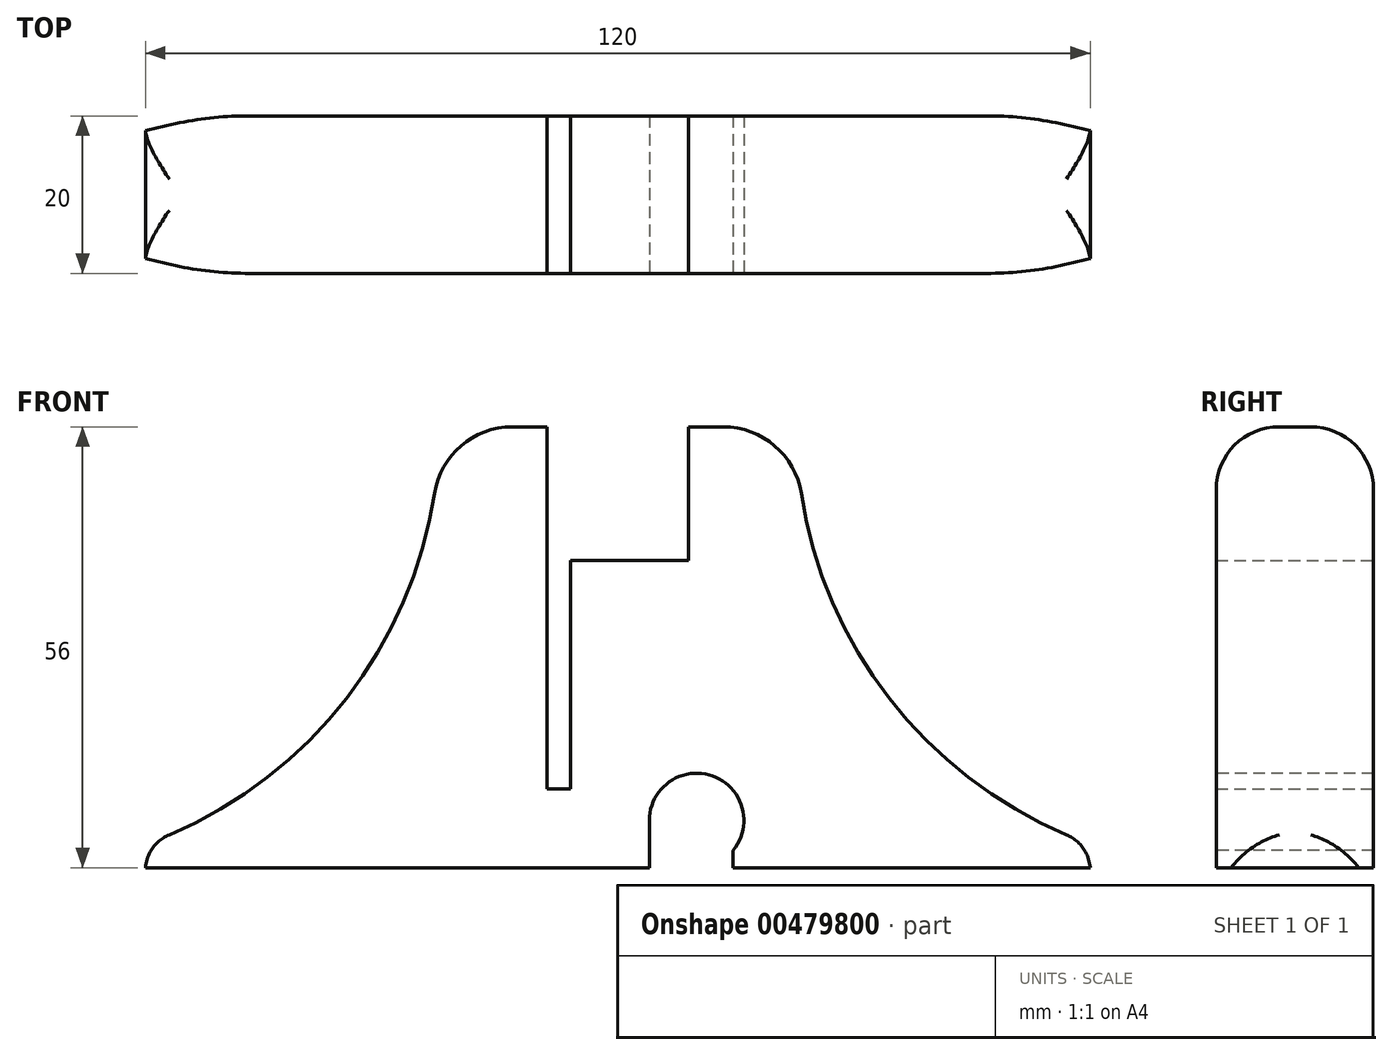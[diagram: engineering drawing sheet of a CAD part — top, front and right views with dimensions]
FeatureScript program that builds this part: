
annotation { "Feature Type Name" : "Feature", "Feature Type Description" : "" }
export const myFeature = defineFeature(function(context is Context, id is Id, definition is map)
    precondition{}
    {
        {
            var Q0;
            Q0=qCreatedBy(makeId("Front.planeOp"),FACE);
            var sketch = newSketch(context, id + "F0", { "sketchPlane" : qUnion([Q0])});
            skLineSegment(sketch, "E0", {"start": v(-9, 56) * mm, "end": v(-9, 10) * mm});
            skLineSegment(sketch, "E1", {"start": v(-9, 10) * mm, "end": v(-6, 10) * mm});
            skLineSegment(sketch, "E2", {"start": v(-6, 10) * mm, "end": v(-6, 39) * mm});
            skLineSegment(sketch, "E3", {"start": v(-6, 39) * mm, "end": v(9, 39) * mm});
            skLineSegment(sketch, "E4", {"start": v(9, 39) * mm, "end": v(9, 56) * mm});
            skLineSegment(sketch, "E5", {"start": v(9, 56) * mm, "end": v(22.65, 56) * mm});
            skLineSegment(sketch, "E6", {"start": v(-9, 56) * mm, "end": v(-22.65, 56) * mm});
            skLineSegment(sketch, "E7", {"start": v(-60, 3) * mm, "end": v(-60, 0) * mm});
            skLineSegment(sketch, "E8", {"start": v(-60, 0) * mm, "end": v(60, 0) * mm});
            skLineSegment(sketch, "E9", {"start": v(60, 0) * mm, "end": v(60, 3) * mm});
            skArc(sketch, "E10", {"start": v(-60, 3) * mm, "mid": v(-32.92, 23.58) * mm, "end": v(-22.65, 56) * mm});
            skArc(sketch, "E11.MirrorC", {"start": v(60, 3) * mm, "mid": v(32.92, 23.58) * mm, "end": v(22.65, 56) * mm});
            skSolve(sketch);
        }
        {
            var Q0;
            Q0 = qSketchRegion(id + "F0", true);
            extrude(context, id + "F1", {"entities" : qUnion([Q0]), "depth" : 20 * mm});
        }
        {
            var Q0;
            Q0=makeQuery(id+"F1.opExtrude","SWEPT_EDGE",EDGE,{"disambiguationData":[OSD([sQuery(id+"F0.wireOp",EDGE,"E6"),sQuery(id+"F0.wireOp",EDGE,"E10")])]});
            var Q1;
            Q1=makeQuery(id+"F1.opExtrude","SWEPT_EDGE",EDGE,{"disambiguationData":[OSD([sQuery(id+"F0.wireOp",EDGE,"E5"),sQuery(id+"F0.wireOp",EDGE,"E11.MirrorC")])]});
            fillet(context, id + "F2", {"entities" : qUnion([Q0, Q1]), "radius" : 10 * mm, "tangentPropagation" : true, "allowEdgeOverflow" : false});
        }
        {
            var Q0;
            Q0=makeQuery(id+"F1.opExtrude","SWEPT_EDGE",EDGE,{"disambiguationData":[OSD([sQuery(id+"F0.wireOp",EDGE,"E7"),sQuery(id+"F0.wireOp",EDGE,"E10")])]});
            var Q1;
            Q1=makeQuery(id+"F1.opExtrude","SWEPT_EDGE",EDGE,{"disambiguationData":[OSD([sQuery(id+"F0.wireOp",EDGE,"E9"),sQuery(id+"F0.wireOp",EDGE,"E11.MirrorC")])]});
            fillet(context, id + "F3", {"entities" : qUnion([Q0, Q1]), "radius" : 5 * mm, "tangentPropagation" : true, "allowEdgeOverflow" : false});
        }
        {
            var Q0;
            {var subQ0=sQuery(id+"F0.wireOp",EDGE,"E10");var subQ1=sQuery(id+"F0.wireOp",EDGE,"E7");Q0=makeQuery(id+"F3.opFillet","BLEND_EDGE",EDGE,{"blendedFrom":[makeQuery(id+"F1.opExtrude","SWEPT_EDGE",EDGE,{"disambiguationData":[OSD([subQ1,subQ0])]}),makeQuery(id+"F1.opExtrude","CAP_FACE",FACE,{"disambiguationData":[OSD([sQuery(id+"F0.wireOp",EDGE,"E0"),sQuery(id+"F0.wireOp",EDGE,"E1"),sQuery(id+"F0.wireOp",EDGE,"E2"),sQuery(id+"F0.wireOp",EDGE,"E3"),sQuery(id+"F0.wireOp",EDGE,"E4"),sQuery(id+"F0.wireOp",EDGE,"E5"),sQuery(id+"F0.wireOp",EDGE,"E6"),subQ1,sQuery(id+"F0.wireOp",EDGE,"E8"),sQuery(id+"F0.wireOp",EDGE,"E9"),subQ0,sQuery(id+"F0.wireOp",EDGE,"E11.MirrorC")])],"isStart":false})],"blendedInto":[makeQuery(id+"F1.opExtrude","CAP_FACE",FACE,{"disambiguationData":[OSD([sQuery(id+"F0.wireOp",EDGE,"E0"),sQuery(id+"F0.wireOp",EDGE,"E1"),sQuery(id+"F0.wireOp",EDGE,"E2"),sQuery(id+"F0.wireOp",EDGE,"E3"),sQuery(id+"F0.wireOp",EDGE,"E4"),sQuery(id+"F0.wireOp",EDGE,"E5"),sQuery(id+"F0.wireOp",EDGE,"E6"),subQ1,sQuery(id+"F0.wireOp",EDGE,"E8"),sQuery(id+"F0.wireOp",EDGE,"E9"),subQ0,sQuery(id+"F0.wireOp",EDGE,"E11.MirrorC")])],"isStart":false})]});}
            var Q1;
            Q1=makeQuery(id+"F1.opExtrude","CAP_EDGE",EDGE,{"disambiguationData":[OSD([sQuery(id+"F0.wireOp",EDGE,"E10")])],"isStart":false});
            var Q2;
            {var subQ0=sQuery(id+"F0.wireOp",EDGE,"E10");var subQ1=sQuery(id+"F0.wireOp",EDGE,"E6");Q2=makeQuery(id+"F2.opFillet","BLEND_EDGE",EDGE,{"blendedFrom":[makeQuery(id+"F1.opExtrude","SWEPT_EDGE",EDGE,{"disambiguationData":[OSD([subQ1,subQ0])]}),makeQuery(id+"F1.opExtrude","CAP_FACE",FACE,{"disambiguationData":[OSD([sQuery(id+"F0.wireOp",EDGE,"E0"),sQuery(id+"F0.wireOp",EDGE,"E1"),sQuery(id+"F0.wireOp",EDGE,"E2"),sQuery(id+"F0.wireOp",EDGE,"E3"),sQuery(id+"F0.wireOp",EDGE,"E4"),sQuery(id+"F0.wireOp",EDGE,"E5"),subQ1,sQuery(id+"F0.wireOp",EDGE,"E7"),sQuery(id+"F0.wireOp",EDGE,"E8"),sQuery(id+"F0.wireOp",EDGE,"E9"),subQ0,sQuery(id+"F0.wireOp",EDGE,"E11.MirrorC")])],"isStart":false})],"blendedInto":[makeQuery(id+"F1.opExtrude","CAP_FACE",FACE,{"disambiguationData":[OSD([sQuery(id+"F0.wireOp",EDGE,"E0"),sQuery(id+"F0.wireOp",EDGE,"E1"),sQuery(id+"F0.wireOp",EDGE,"E2"),sQuery(id+"F0.wireOp",EDGE,"E3"),sQuery(id+"F0.wireOp",EDGE,"E4"),sQuery(id+"F0.wireOp",EDGE,"E5"),subQ1,sQuery(id+"F0.wireOp",EDGE,"E7"),sQuery(id+"F0.wireOp",EDGE,"E8"),sQuery(id+"F0.wireOp",EDGE,"E9"),subQ0,sQuery(id+"F0.wireOp",EDGE,"E11.MirrorC")])],"isStart":false})]});}
            var Q3;
            Q3=makeQuery(id+"F1.opExtrude","CAP_EDGE",EDGE,{"disambiguationData":[OSD([sQuery(id+"F0.wireOp",EDGE,"E6")])],"isStart":false});
            var Q4;
            Q4=makeQuery(id+"F1.opExtrude","CAP_EDGE",EDGE,{"disambiguationData":[OSD([sQuery(id+"F0.wireOp",EDGE,"E5")])],"isStart":false});
            var Q5;
            {var subQ0=sQuery(id+"F0.wireOp",EDGE,"E11.MirrorC");var subQ1=sQuery(id+"F0.wireOp",EDGE,"E5");Q5=makeQuery(id+"F2.opFillet","BLEND_EDGE",EDGE,{"blendedFrom":[makeQuery(id+"F1.opExtrude","SWEPT_EDGE",EDGE,{"disambiguationData":[OSD([subQ1,subQ0])]}),makeQuery(id+"F1.opExtrude","CAP_FACE",FACE,{"disambiguationData":[OSD([sQuery(id+"F0.wireOp",EDGE,"E0"),sQuery(id+"F0.wireOp",EDGE,"E1"),sQuery(id+"F0.wireOp",EDGE,"E2"),sQuery(id+"F0.wireOp",EDGE,"E3"),sQuery(id+"F0.wireOp",EDGE,"E4"),subQ1,sQuery(id+"F0.wireOp",EDGE,"E6"),sQuery(id+"F0.wireOp",EDGE,"E7"),sQuery(id+"F0.wireOp",EDGE,"E8"),sQuery(id+"F0.wireOp",EDGE,"E9"),sQuery(id+"F0.wireOp",EDGE,"E10"),subQ0])],"isStart":false})],"blendedInto":[makeQuery(id+"F1.opExtrude","CAP_FACE",FACE,{"disambiguationData":[OSD([sQuery(id+"F0.wireOp",EDGE,"E0"),sQuery(id+"F0.wireOp",EDGE,"E1"),sQuery(id+"F0.wireOp",EDGE,"E2"),sQuery(id+"F0.wireOp",EDGE,"E3"),sQuery(id+"F0.wireOp",EDGE,"E4"),subQ1,sQuery(id+"F0.wireOp",EDGE,"E6"),sQuery(id+"F0.wireOp",EDGE,"E7"),sQuery(id+"F0.wireOp",EDGE,"E8"),sQuery(id+"F0.wireOp",EDGE,"E9"),sQuery(id+"F0.wireOp",EDGE,"E10"),subQ0])],"isStart":false})]});}
            var Q6;
            Q6=makeQuery(id+"F1.opExtrude","CAP_EDGE",EDGE,{"disambiguationData":[OSD([sQuery(id+"F0.wireOp",EDGE,"E11.MirrorC")])],"isStart":false});
            var Q7;
            {var subQ0=sQuery(id+"F0.wireOp",EDGE,"E11.MirrorC");var subQ1=sQuery(id+"F0.wireOp",EDGE,"E9");Q7=makeQuery(id+"F3.opFillet","BLEND_EDGE",EDGE,{"blendedFrom":[makeQuery(id+"F1.opExtrude","SWEPT_EDGE",EDGE,{"disambiguationData":[OSD([subQ1,subQ0])]}),makeQuery(id+"F1.opExtrude","CAP_FACE",FACE,{"disambiguationData":[OSD([sQuery(id+"F0.wireOp",EDGE,"E0"),sQuery(id+"F0.wireOp",EDGE,"E1"),sQuery(id+"F0.wireOp",EDGE,"E2"),sQuery(id+"F0.wireOp",EDGE,"E3"),sQuery(id+"F0.wireOp",EDGE,"E4"),sQuery(id+"F0.wireOp",EDGE,"E5"),sQuery(id+"F0.wireOp",EDGE,"E6"),sQuery(id+"F0.wireOp",EDGE,"E7"),sQuery(id+"F0.wireOp",EDGE,"E8"),subQ1,sQuery(id+"F0.wireOp",EDGE,"E10"),subQ0])],"isStart":false})],"blendedInto":[makeQuery(id+"F1.opExtrude","CAP_FACE",FACE,{"disambiguationData":[OSD([sQuery(id+"F0.wireOp",EDGE,"E0"),sQuery(id+"F0.wireOp",EDGE,"E1"),sQuery(id+"F0.wireOp",EDGE,"E2"),sQuery(id+"F0.wireOp",EDGE,"E3"),sQuery(id+"F0.wireOp",EDGE,"E4"),sQuery(id+"F0.wireOp",EDGE,"E5"),sQuery(id+"F0.wireOp",EDGE,"E6"),sQuery(id+"F0.wireOp",EDGE,"E7"),sQuery(id+"F0.wireOp",EDGE,"E8"),subQ1,sQuery(id+"F0.wireOp",EDGE,"E10"),subQ0])],"isStart":false})]});}
            var Q8;
            {var subQ0=sQuery(id+"F0.wireOp",EDGE,"E11.MirrorC");var subQ1=sQuery(id+"F0.wireOp",EDGE,"E9");Q8=makeQuery(id+"F3.opFillet","BLEND_EDGE",EDGE,{"blendedFrom":[makeQuery(id+"F1.opExtrude","SWEPT_EDGE",EDGE,{"disambiguationData":[OSD([subQ1,subQ0])]}),makeQuery(id+"F1.opExtrude","CAP_FACE",FACE,{"disambiguationData":[OSD([sQuery(id+"F0.wireOp",EDGE,"E0"),sQuery(id+"F0.wireOp",EDGE,"E1"),sQuery(id+"F0.wireOp",EDGE,"E2"),sQuery(id+"F0.wireOp",EDGE,"E3"),sQuery(id+"F0.wireOp",EDGE,"E4"),sQuery(id+"F0.wireOp",EDGE,"E5"),sQuery(id+"F0.wireOp",EDGE,"E6"),sQuery(id+"F0.wireOp",EDGE,"E7"),sQuery(id+"F0.wireOp",EDGE,"E8"),subQ1,sQuery(id+"F0.wireOp",EDGE,"E10"),subQ0])],"isStart":true})],"blendedInto":[makeQuery(id+"F1.opExtrude","CAP_FACE",FACE,{"disambiguationData":[OSD([sQuery(id+"F0.wireOp",EDGE,"E0"),sQuery(id+"F0.wireOp",EDGE,"E1"),sQuery(id+"F0.wireOp",EDGE,"E2"),sQuery(id+"F0.wireOp",EDGE,"E3"),sQuery(id+"F0.wireOp",EDGE,"E4"),sQuery(id+"F0.wireOp",EDGE,"E5"),sQuery(id+"F0.wireOp",EDGE,"E6"),sQuery(id+"F0.wireOp",EDGE,"E7"),sQuery(id+"F0.wireOp",EDGE,"E8"),subQ1,sQuery(id+"F0.wireOp",EDGE,"E10"),subQ0])],"isStart":true})]});}
            var Q9;
            {var subQ0=sQuery(id+"F0.wireOp",EDGE,"E10");var subQ1=sQuery(id+"F0.wireOp",EDGE,"E7");Q9=makeQuery(id+"F3.opFillet","BLEND_EDGE",EDGE,{"blendedFrom":[makeQuery(id+"F1.opExtrude","SWEPT_EDGE",EDGE,{"disambiguationData":[OSD([subQ1,subQ0])]}),makeQuery(id+"F1.opExtrude","CAP_FACE",FACE,{"disambiguationData":[OSD([sQuery(id+"F0.wireOp",EDGE,"E0"),sQuery(id+"F0.wireOp",EDGE,"E1"),sQuery(id+"F0.wireOp",EDGE,"E2"),sQuery(id+"F0.wireOp",EDGE,"E3"),sQuery(id+"F0.wireOp",EDGE,"E4"),sQuery(id+"F0.wireOp",EDGE,"E5"),sQuery(id+"F0.wireOp",EDGE,"E6"),subQ1,sQuery(id+"F0.wireOp",EDGE,"E8"),sQuery(id+"F0.wireOp",EDGE,"E9"),subQ0,sQuery(id+"F0.wireOp",EDGE,"E11.MirrorC")])],"isStart":true})],"blendedInto":[makeQuery(id+"F1.opExtrude","CAP_FACE",FACE,{"disambiguationData":[OSD([sQuery(id+"F0.wireOp",EDGE,"E0"),sQuery(id+"F0.wireOp",EDGE,"E1"),sQuery(id+"F0.wireOp",EDGE,"E2"),sQuery(id+"F0.wireOp",EDGE,"E3"),sQuery(id+"F0.wireOp",EDGE,"E4"),sQuery(id+"F0.wireOp",EDGE,"E5"),sQuery(id+"F0.wireOp",EDGE,"E6"),subQ1,sQuery(id+"F0.wireOp",EDGE,"E8"),sQuery(id+"F0.wireOp",EDGE,"E9"),subQ0,sQuery(id+"F0.wireOp",EDGE,"E11.MirrorC")])],"isStart":true})]});}
            fillet(context, id + "F4", {"entities" : qUnion([Q0, Q1, Q2, Q3, Q4, Q5, Q6, Q7, Q8, Q9]), "radius" : 8 * mm, "tangentPropagation" : true, "allowEdgeOverflow" : false});
        }
        {
            var Q0;
            Q0=makeQuery(id+"F1.opExtrude","CAP_FACE",FACE,{"disambiguationData":[OSD([sQuery(id+"F0.wireOp",EDGE,"E0"),sQuery(id+"F0.wireOp",EDGE,"E1"),sQuery(id+"F0.wireOp",EDGE,"E2"),sQuery(id+"F0.wireOp",EDGE,"E3"),sQuery(id+"F0.wireOp",EDGE,"E4"),sQuery(id+"F0.wireOp",EDGE,"E5"),sQuery(id+"F0.wireOp",EDGE,"E6"),sQuery(id+"F0.wireOp",EDGE,"E7"),sQuery(id+"F0.wireOp",EDGE,"E8"),sQuery(id+"F0.wireOp",EDGE,"E9"),sQuery(id+"F0.wireOp",EDGE,"E10"),sQuery(id+"F0.wireOp",EDGE,"E11.MirrorC")])],"isStart":false});
            var sketch = newSketch(context, id + "F5", { "sketchPlane" : qUnion([Q0])});
            skArc(sketch, "E12", {"start": v(14.65, 2.2) * mm, "mid": v(12.01, 11.65) * mm, "end": v(4, 6) * mm});
            skLineSegment(sketch, "E13", {"start": v(4, 6) * mm, "end": v(4, 0) * mm});
            skLineSegment(sketch, "E14", {"start": v(14.65, 2.2) * mm, "end": v(14.65, 0) * mm});
            skLineSegment(sketch, "E15", {"start": v(4, 0) * mm, "end": v(14.65, 0) * mm});
            skSolve(sketch);
        }
        {
            var Q0;
            Q0 = qSketchRegion(id + "F5", true);
            extrude(context, id + "F6", {"entities" : qUnion([Q0]), "operationType" : NewBodyOperationType.REMOVE, "oppositeDirection" : true, "depth" : 25 * mm});
        }
    });
